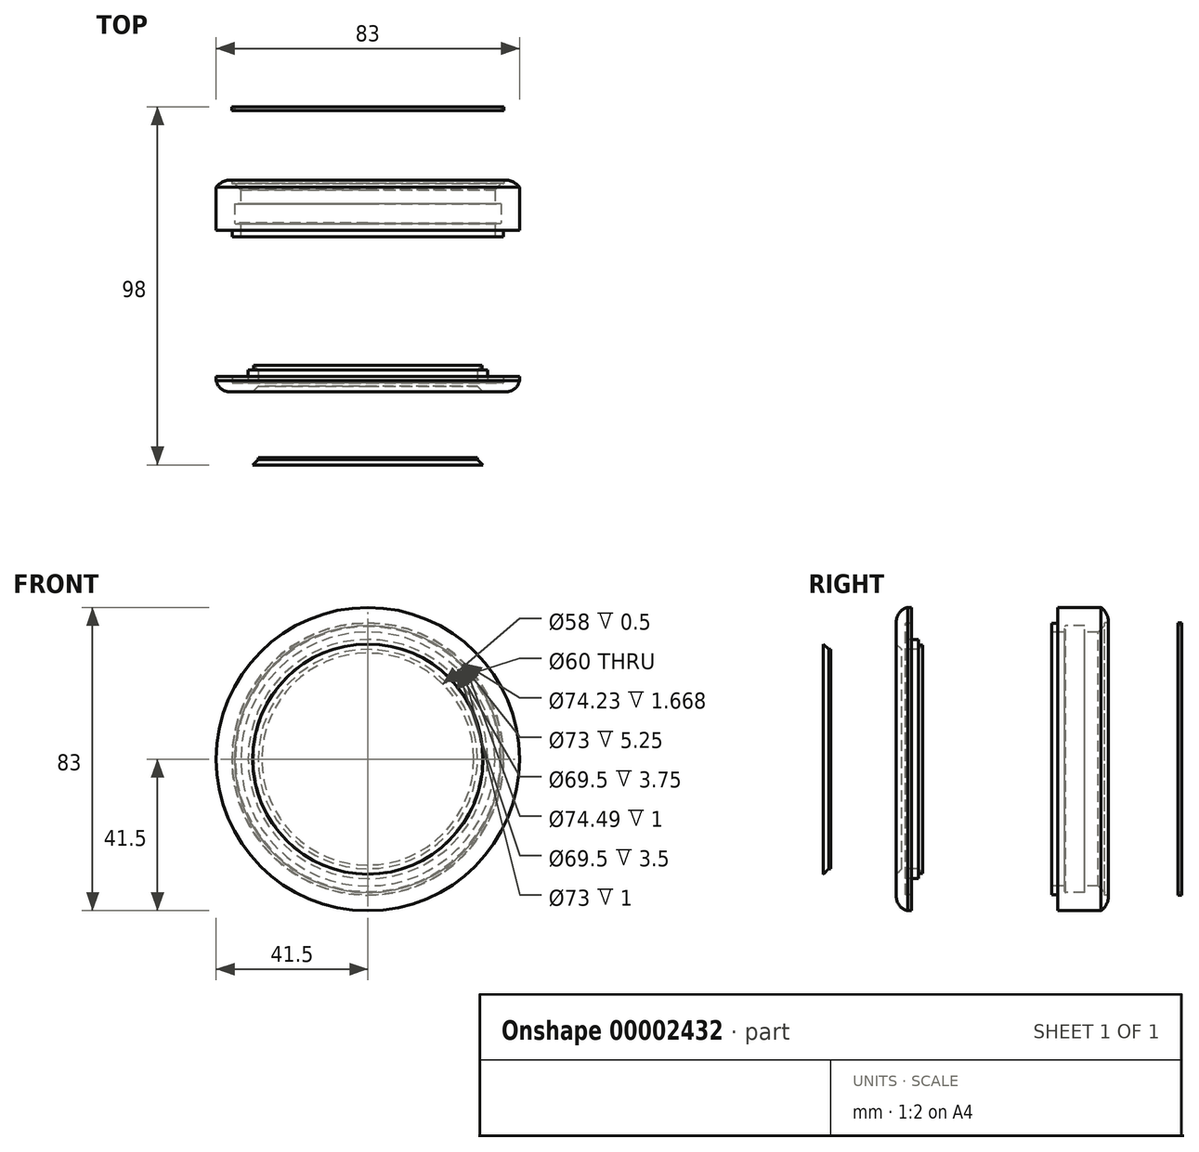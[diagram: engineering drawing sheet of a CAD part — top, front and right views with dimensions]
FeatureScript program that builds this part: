
annotation { "Feature Type Name" : "Feature", "Feature Type Description" : "" }
export const myFeature = defineFeature(function(context is Context, id is Id, definition is map)
    precondition{}
    {
        {
            var Q0;
            Q0=qCreatedBy(makeId("Top.planeOp"),FACE);
            var sketch = newSketch(context, id + "F0", { "sketchPlane" : qUnion([Q0])});
            skLineSegment(sketch, "E0", {"start": v(-33.25, 2.75) * mm, "end": v(-34.25, 2.75) * mm});
            skLineSegment(sketch, "E1.bottom", {"start": v(-34.25, 11.25) * mm, "end": v(-36, 11.25) * mm});
            skLineSegment(sketch, "E1.top", {"start": v(-34.25, 6.25) * mm, "end": v(-36, 6.25) * mm});
            skLineSegment(sketch, "E1.right", {"start": v(-36, 11.25) * mm, "end": v(-36, 6.25) * mm});
            skLineSegment(sketch, "E2.bottom", {"start": v(-33.25, 11.25) * mm, "end": v(-31.5, 11.25) * mm});
            skLineSegment(sketch, "E2.top", {"start": v(-33.25, 6.25) * mm, "end": v(-31.5, 6.25) * mm});
            skLineSegment(sketch, "E2.right", {"start": v(-31.5, 11.25) * mm, "end": v(-31.5, 6.25) * mm});
            skLineSegment(sketch, "E3", {"start": v(-41.5, 16) * mm, "end": v(-40, 16) * mm});
            skLineSegment(sketch, "E4", {"start": v(-40, 16) * mm, "end": v(-40, 9.75) * mm});
            skLineSegment(sketch, "E5", {"start": v(-40, 9.75) * mm, "end": v(-36.5, 6.25) * mm});
            skLineSegment(sketch, "E6", {"start": v(-36.5, 6.25) * mm, "end": v(-36.5, 9.75) * mm});
            skLineSegment(sketch, "E7", {"start": v(-36.5, 9.75) * mm, "end": v(-36.5, 11.5) * mm});
            skArc(sketch, "E8", {"start": v(-37.25, 18) * mm, "mid": v(-39.62, 17.53) * mm, "end": v(-41.5, 16) * mm});
            skLineSegment(sketch, "E9", {"start": v(-41.5, 16) * mm, "end": v(-41.5, 4.17) * mm});
            skLineSegment(sketch, "E10", {"start": v(-34.75, 2.5) * mm, "end": v(-34.75, 6) * mm});
            skLineSegment(sketch, "E11", {"start": v(-34.75, 6) * mm, "end": v(-36.25, 6) * mm});
            skLineSegment(sketch, "E12", {"start": v(-36.25, 6) * mm, "end": v(-40, 9.75) * mm});
            skLineSegment(sketch, "E13", {"start": v(-40, 9.75) * mm, "end": v(-40, 16) * mm});
            skLineSegment(sketch, "E14", {"start": v(-33.25, 14.75) * mm, "end": v(-33.25, 11.25) * mm});
            skLineSegment(sketch, "E15", {"start": v(-34.25, 14.75) * mm, "end": v(-34.25, 11.25) * mm});
            skLineSegment(sketch, "E16", {"start": v(-34.25, 6.25) * mm, "end": v(-34.25, 11.25) * mm});
            skLineSegment(sketch, "E17", {"start": v(-33.25, 2.75) * mm, "end": v(-33.25, 6.25) * mm});
            skLineSegment(sketch, "E18", {"start": v(-33.25, 11.25) * mm, "end": v(-33.25, 6.25) * mm});
            skLineSegment(sketch, "E19", {"start": v(-34.25, 6.25) * mm, "end": v(-34.25, 2.75) * mm});
            skLineSegment(sketch, "E20", {"start": v(-41.5, 0) * mm, "end": v(41.5, 0) * mm, "construction": true});
            skLineSegment(sketch, "E21", {"start": v(-41.5, 4.17) * mm, "end": v(-41.5, 3.08) * mm});
            skLineSegment(sketch, "E22", {"start": v(-37.68, 0) * mm, "end": v(0, 0) * mm});
            skLineSegment(sketch, "E23", {"start": v(-34.75, 2.5) * mm, "end": v(-32.75, 2.5) * mm});
            skLineSegment(sketch, "E24", {"start": v(-32.75, 2.5) * mm, "end": v(-32.75, 6) * mm});
            skLineSegment(sketch, "E25", {"start": v(-32.75, 6) * mm, "end": v(-31.23, 6) * mm});
            skLineSegment(sketch, "E26", {"start": v(-31.23, 6) * mm, "end": v(-31.23, 7.23) * mm});
            skLineSegment(sketch, "E27", {"start": v(-30, 6) * mm, "end": v(-30, 1.5) * mm});
            skLineSegment(sketch, "E28", {"start": v(0, 1.5) * mm, "end": v(0, 0) * mm});
            skLineSegment(sketch, "E29", {"start": v(-40, 9.75) * mm, "end": v(-36.5, 9.75) * mm, "construction": true});
            skLineSegment(sketch, "E30", {"start": v(-36.5, 6.25) * mm, "end": v(-36, 6.25) * mm, "construction": true});
            skLineSegment(sketch, "E31", {"start": v(-41.5, 0) * mm, "end": v(-41.5, 18) * mm, "construction": true});
            skLineSegment(sketch, "E32", {"start": v(-33.52, 15) * mm, "end": v(-33.52, 14.75) * mm, "construction": true});
            skLineSegment(sketch, "E33", {"start": v(-33.75, 2.75) * mm, "end": v(-33.75, 2.5) * mm, "construction": true});
            skLineSegment(sketch, "E34", {"start": v(-37.25, 17) * mm, "end": v(-36.5, 17) * mm});
            skLineSegment(sketch, "E35", {"start": v(-41.5, 4.17) * mm, "end": v(-40.2, 4.17) * mm});
            skLineSegment(sketch, "E36", {"start": v(-40.2, 4.17) * mm, "end": v(-37.12, 4.17) * mm});
            skLineSegment(sketch, "E37", {"start": v(-37.12, 2.5) * mm, "end": v(-37.12, 4.17) * mm});
            skLineSegment(sketch, "E38", {"start": v(-37.12, 2.5) * mm, "end": v(-34.75, 2.5) * mm});
            skLineSegment(sketch, "E39", {"start": v(-33.25, 2.5) * mm, "end": v(-33.25, 0) * mm, "construction": true});
            skLineSegment(sketch, "E40", {"start": v(-44.1, 18) * mm, "end": v(-44.1, 17) * mm, "construction": true});
            skLineSegment(sketch, "E41", {"start": v(-44.1, 17) * mm, "end": v(-44.1, 16) * mm, "construction": true});
            skLineSegment(sketch, "E42", {"start": v(-44.1, 2.5) * mm, "end": v(-44.1, 1.5) * mm, "construction": true});
            skLineSegment(sketch, "E43", {"start": v(-44.1, 16) * mm, "end": v(-44.1, 11.5) * mm, "construction": true});
            skLineSegment(sketch, "E44", {"start": v(-44.1, 4.17) * mm, "end": v(-44.1, 2.5) * mm, "construction": true});
            skLineSegment(sketch, "E45", {"start": v(-37.25, 18) * mm, "end": v(-37.25, 17) * mm});
            skLineSegment(sketch, "E46", {"start": v(-41.5, 21.17) * mm, "end": v(-37.25, 21.17) * mm, "construction": true});
            skLineSegment(sketch, "E47", {"start": v(-37.25, 21.17) * mm, "end": v(-34.75, 21.17) * mm, "construction": true});
            skLineSegment(sketch, "E48", {"start": v(-34.75, 21.17) * mm, "end": v(-32.75, 21.17) * mm, "construction": true});
            skLineSegment(sketch, "E49", {"start": v(-30, 21.17) * mm, "end": v(-23.5, 21.17) * mm, "construction": true});
            skLineSegment(sketch, "E50", {"start": v(-23.5, 21.17) * mm, "end": v(0, 21.17) * mm, "construction": true});
            skLineSegment(sketch, "E51", {"start": v(-30, 6) * mm, "end": v(-31.23, 7.23) * mm});
            skLineSegment(sketch, "E52", {"start": v(-33.25, 4.5) * mm, "end": v(-32.75, 4.5) * mm, "construction": true});
            skLineSegment(sketch, "E53", {"start": v(-34.25, 4.5) * mm, "end": v(-34.75, 4.5) * mm, "construction": true});
            skLineSegment(sketch, "E54", {"start": v(-30, 1.5) * mm, "end": v(-31.5, 0) * mm});
            skLineSegment(sketch, "E55", {"start": v(0, 0) * mm, "end": v(0, 18) * mm, "construction": true});
            skLineSegment(sketch, "E56", {"start": v(-34.75, 11.5) * mm, "end": v(-36.5, 11.5) * mm});
            skLineSegment(sketch, "E57", {"start": v(-34.75, 11.5) * mm, "end": v(-34.75, 15.25) * mm});
            skLineSegment(sketch, "E58", {"start": v(-34.75, 15.25) * mm, "end": v(-36.5, 17) * mm});
            skLineSegment(sketch, "E59", {"start": v(-33.25, 14.75) * mm, "end": v(-34.25, 14.75) * mm});
            skLineSegment(sketch, "E60", {"start": v(-44.1, 6) * mm, "end": v(-44.1, 4.17) * mm, "construction": true});
            skLineSegment(sketch, "E61", {"start": v(-44.1, 7.23) * mm, "end": v(-44.1, 6) * mm, "construction": true});
            skLineSegment(sketch, "E62", {"start": v(-44.1, 7.23) * mm, "end": v(-31.23, 7.23) * mm, "construction": true});
            skLineSegment(sketch, "E63", {"start": v(-44.1, 11.25) * mm, "end": v(-44.1, 7.23) * mm, "construction": true});
            skLineSegment(sketch, "E64", {"start": v(-44.1, 11.5) * mm, "end": v(-44.1, 11.25) * mm, "construction": true});
            skLineSegment(sketch, "E65", {"start": v(-47.67, 11.5) * mm, "end": v(-47.67, 6) * mm, "construction": true});
            skLineSegment(sketch, "E66", {"start": v(-30, 1.5) * mm, "end": v(-30, 2) * mm});
            skLineSegment(sketch, "E67", {"start": v(-30, 2) * mm, "end": v(-29, 2) * mm});
            skLineSegment(sketch, "E68", {"start": v(-29, 2) * mm, "end": v(-29, 1.5) * mm});
            skLineSegment(sketch, "E69", {"start": v(-29, 1.5) * mm, "end": v(0, 1.5) * mm});
            skLineSegment(sketch, "E70", {"start": v(-37.25, 18) * mm, "end": v(0, 18) * mm});
            skLineSegment(sketch, "E71", {"start": v(0, 18) * mm, "end": v(0, 15.25) * mm});
            skLineSegment(sketch, "E72", {"start": v(0, 15.25) * mm, "end": v(-34.75, 15.25) * mm});
            skLineSegment(sketch, "E73", {"start": v(-44.1, 1.5) * mm, "end": v(-44.1, 0) * mm, "construction": true});
            skLineSegment(sketch, "E74", {"start": v(-47.34, 0) * mm, "end": v(-47.34, 2.5) * mm, "construction": true});
            skArc(sketch, "E75", {"start": v(-41.5, 3.08) * mm, "mid": v(-40.13, 0.87) * mm, "end": v(-37.68, 0) * mm});
            skLineSegment(sketch, "E76", {"start": v(-32.75, 21.17) * mm, "end": v(-30, 21.17) * mm, "construction": true});
            skLineSegment(sketch, "E77", {"start": v(-36.5, 11.5) * mm, "end": v(-40, 11.5) * mm});
            skLineSegment(sketch, "E78", {"start": v(-36.5, 17) * mm, "end": v(-36.5, 18) * mm});
            skLineSegment(sketch, "E79", {"start": v(-36.5, 18) * mm, "end": v(-7.22, 18) * mm});
            skLineSegment(sketch, "E80", {"start": v(-7.22, 18) * mm, "end": v(-7.22, 19.47) * mm});
            skLineSegment(sketch, "E81", {"start": v(-7.22, 19.47) * mm, "end": v(-35.97, 19.47) * mm});
            skLineSegment(sketch, "E82", {"start": v(-35.97, 19.47) * mm, "end": v(-37.25, 18) * mm});
            skSolve(sketch);
        }
        {
            var Q0;
            Q0=makeQuery(id+"F0.imprint","IMPRINT",FACE,{"disambiguationData":[TD([[makeQuery(id+"F0.imprint","IMPRINT",EDGE,{"derivedFrom":sQuery(id+"F0.wireOp",EDGE,"E34")}),1.0]])]});
            var Q1;
            Q1=sQuery(id+"F0.wireOp",EDGE,"E55");
            revolve(context, id + "F1", {"entities" : qUnion([Q0]), "axis" : qUnion([Q1]), "revolveType" : RevolveType.FULL});
        }
        {
            var Q0;
            {var subQ2=sQuery(id+"F0.wireOp",EDGE,"E3");Q0=makeQuery(id+"F0.imprint","IMPRINT",FACE,{"disambiguationData":[TD([[makeQuery(id+"F0.imprint","IMPRINT",EDGE,{"derivedFrom":subQ2}),1.0]])]});}
            var Q1;
            {var subQ4=sQuery(id+"F0.wireOp",EDGE,"E6");Q1=makeQuery(id+"F0.imprint","IMPRINT",FACE,{"disambiguationData":[TD([[makeQuery(id+"F0.imprint","IMPRINT",EDGE,{"derivedFrom":subQ4}),1.0]])]});}
            var Q2;
            Q2=sQuery(id+"F0.wireOp",EDGE,"E55");
            revolve(context, id + "F2", {"entities" : qUnion([Q0, Q1]), "axis" : qUnion([Q2]), "revolveType" : RevolveType.FULL});
        }
        {
            var Q0;
            {var subQ2=sQuery(id+"F0.wireOp",EDGE,"E3");Q0=makeQuery(id+"F0.imprint","IMPRINT",FACE,{"disambiguationData":[TD([[makeQuery(id+"F0.imprint","IMPRINT",EDGE,{"derivedFrom":subQ2}),-1.0]])]});}
            var Q1;
            Q1=sQuery(id+"F0.wireOp",EDGE,"E9");
            var Q2;
            Q2=sQuery(id+"F0.wireOp",EDGE,"E3");
            var Q3;
            Q3=sQuery(id+"F0.wireOp",EDGE,"E4");
            var Q4;
            Q4=sQuery(id+"F0.wireOp",EDGE,"E5");
            var Q5;
            Q5=sQuery(id+"F0.wireOp",EDGE,"E11");
            var Q6;
            Q6=sQuery(id+"F0.wireOp",EDGE,"E10");
            var Q7;
            Q7=sQuery(id+"F0.wireOp",EDGE,"E38");
            var Q8;
            Q8=sQuery(id+"F0.wireOp",EDGE,"E37");
            var Q9;
            Q9=sQuery(id+"F0.wireOp",EDGE,"E36");
            var Q10;
            Q10=sQuery(id+"F0.wireOp",EDGE,"E35");
            var Q11;
            Q11=sQuery(id+"F0.wireOp",EDGE,"E55");
            revolve(context, id + "F3", {"operationType" : NewBodyOperationType.ADD, "entities" : qUnion([Q0]), "surfaceEntities" : qUnion([Q1, Q2, Q3, Q4, Q5, Q6, Q7, Q8, Q9, Q10]), "axis" : qUnion([Q11]), "revolveType" : RevolveType.FULL});
        }
        {
            var Q0;
            Q0=makeQuery(id+"F0.imprint","IMPRINT",FACE,{"disambiguationData":[TD([[makeQuery(id+"F0.imprint","IMPRINT",EDGE,{"derivedFrom":sQuery(id+"F0.wireOp",EDGE,"E21")}),1.0]])]});
            var Q1;
            Q1=sQuery(id+"F0.wireOp",EDGE,"E55");
            revolve(context, id + "F4", {"entities" : qUnion([Q0]), "axis" : qUnion([Q1]), "revolveType" : RevolveType.FULL});
        }
        {
            var Q0;
            {var subQ1=sQuery(id+"F0.wireOp",EDGE,"E28");Q0=makeQuery(id+"F0.imprint","IMPRINT",FACE,{"disambiguationData":[TD([[makeQuery(id+"F0.imprint","IMPRINT",EDGE,{"derivedFrom":subQ1}),-1.0]])]});}
            var Q1;
            Q1=sQuery(id+"F0.wireOp",EDGE,"E55");
            revolve(context, id + "F5", {"entities" : qUnion([Q0]), "axis" : qUnion([Q1]), "revolveType" : RevolveType.FULL});
        }
        {
            var Q0;
            Q0=makeQuery(id+"F4.opRevolve","SWEPT_BODY",BODY,{"disambiguationData":[OSD([sQuery(id+"F0.wireOp",EDGE,"E21"),sQuery(id+"F0.wireOp",EDGE,"E22"),sQuery(id+"F0.wireOp",EDGE,"E23"),sQuery(id+"F0.wireOp",EDGE,"E24"),sQuery(id+"F0.wireOp",EDGE,"E25"),sQuery(id+"F0.wireOp",EDGE,"E26"),sQuery(id+"F0.wireOp",EDGE,"E27"),sQuery(id+"F0.wireOp",EDGE,"E35"),sQuery(id+"F0.wireOp",EDGE,"E36"),sQuery(id+"F0.wireOp",EDGE,"E37"),sQuery(id+"F0.wireOp",EDGE,"E38"),sQuery(id+"F0.wireOp",EDGE,"E51"),sQuery(id+"F0.wireOp",EDGE,"E54"),sQuery(id+"F0.wireOp",EDGE,"E66"),sQuery(id+"F0.wireOp",EDGE,"E75")])]});
            var Q1;
            Q1=makeQuery(id+"F3.opRevolve","SWEPT_BODY",BODY,{"disambiguationData":[OSD([sQuery(id+"F0.wireOp",EDGE,"E3"),sQuery(id+"F0.wireOp",EDGE,"E9"),sQuery(id+"F0.wireOp",EDGE,"E10"),sQuery(id+"F0.wireOp",EDGE,"E11"),sQuery(id+"F0.wireOp",EDGE,"E12"),sQuery(id+"F0.wireOp",EDGE,"E13"),sQuery(id+"F0.wireOp",EDGE,"E35"),sQuery(id+"F0.wireOp",EDGE,"E36"),sQuery(id+"F0.wireOp",EDGE,"E37"),sQuery(id+"F0.wireOp",EDGE,"E38")])]});
            var Q2;
            Q2=makeQuery(id+"F2.opRevolve","SWEPT_BODY",BODY,{"disambiguationData":[OSD([sQuery(id+"F0.wireOp",EDGE,"E3"),sQuery(id+"F0.wireOp",EDGE,"E6"),sQuery(id+"F0.wireOp",EDGE,"E7"),sQuery(id+"F0.wireOp",EDGE,"E8"),sQuery(id+"F0.wireOp",EDGE,"E12"),sQuery(id+"F0.wireOp",EDGE,"E13"),sQuery(id+"F0.wireOp",EDGE,"E34"),sQuery(id+"F0.wireOp",EDGE,"E45"),sQuery(id+"F0.wireOp",EDGE,"E56"),sQuery(id+"F0.wireOp",EDGE,"E57"),sQuery(id+"F0.wireOp",EDGE,"E58")])]});
            var Q3;
            Q3=makeQuery(id+"F1.opRevolve","SWEPT_BODY",BODY,{"disambiguationData":[OSD([sQuery(id+"F0.wireOp",EDGE,"E34"),sQuery(id+"F0.wireOp",EDGE,"E45"),sQuery(id+"F0.wireOp",EDGE,"E70"),sQuery(id+"F0.wireOp",EDGE,"E78")])]});
            transform(context, id + "F6", {"entities" : qUnion([Q0, Q1, Q2, Q3]), "transformType" : TransformType.TRANSLATION_3D, "dx" : 0 * mm, "dy" : 20 * mm, "dz" : 0 * mm, "makeCopy" : false});
        }
        {
            var Q0;
            Q0=makeQuery(id+"F3.opRevolve","SWEPT_BODY",BODY,{"disambiguationData":[OSD([sQuery(id+"F0.wireOp",EDGE,"E3"),sQuery(id+"F0.wireOp",EDGE,"E9"),sQuery(id+"F0.wireOp",EDGE,"E10"),sQuery(id+"F0.wireOp",EDGE,"E11"),sQuery(id+"F0.wireOp",EDGE,"E12"),sQuery(id+"F0.wireOp",EDGE,"E13"),sQuery(id+"F0.wireOp",EDGE,"E35"),sQuery(id+"F0.wireOp",EDGE,"E36"),sQuery(id+"F0.wireOp",EDGE,"E37"),sQuery(id+"F0.wireOp",EDGE,"E38")])]});
            var Q1;
            Q1=makeQuery(id+"F1.opRevolve","SWEPT_BODY",BODY,{"disambiguationData":[OSD([sQuery(id+"F0.wireOp",EDGE,"E34"),sQuery(id+"F0.wireOp",EDGE,"E45"),sQuery(id+"F0.wireOp",EDGE,"E70"),sQuery(id+"F0.wireOp",EDGE,"E78")])]});
            var Q2;
            Q2=makeQuery(id+"F2.opRevolve","SWEPT_BODY",BODY,{"disambiguationData":[OSD([sQuery(id+"F0.wireOp",EDGE,"E3"),sQuery(id+"F0.wireOp",EDGE,"E6"),sQuery(id+"F0.wireOp",EDGE,"E7"),sQuery(id+"F0.wireOp",EDGE,"E8"),sQuery(id+"F0.wireOp",EDGE,"E12"),sQuery(id+"F0.wireOp",EDGE,"E13"),sQuery(id+"F0.wireOp",EDGE,"E34"),sQuery(id+"F0.wireOp",EDGE,"E45"),sQuery(id+"F0.wireOp",EDGE,"E56"),sQuery(id+"F0.wireOp",EDGE,"E57"),sQuery(id+"F0.wireOp",EDGE,"E58")])]});
            transform(context, id + "F7", {"entities" : qUnion([Q0, Q1, Q2]), "transformType" : TransformType.TRANSLATION_3D, "dx" : 0 * mm, "dy" : 20 * mm, "dz" : 0 * mm, "makeCopy" : false});
        }
        {
            var Q0;
            Q0=makeQuery(id+"F1.opRevolve","SWEPT_BODY",BODY,{"disambiguationData":[OSD([sQuery(id+"F0.wireOp",EDGE,"E34"),sQuery(id+"F0.wireOp",EDGE,"E45"),sQuery(id+"F0.wireOp",EDGE,"E70"),sQuery(id+"F0.wireOp",EDGE,"E78")])]});
            var Q1;
            Q1=makeQuery(id+"F2.opRevolve","SWEPT_BODY",BODY,{"disambiguationData":[OSD([sQuery(id+"F0.wireOp",EDGE,"E3"),sQuery(id+"F0.wireOp",EDGE,"E6"),sQuery(id+"F0.wireOp",EDGE,"E7"),sQuery(id+"F0.wireOp",EDGE,"E8"),sQuery(id+"F0.wireOp",EDGE,"E12"),sQuery(id+"F0.wireOp",EDGE,"E13"),sQuery(id+"F0.wireOp",EDGE,"E34"),sQuery(id+"F0.wireOp",EDGE,"E45"),sQuery(id+"F0.wireOp",EDGE,"E56"),sQuery(id+"F0.wireOp",EDGE,"E57"),sQuery(id+"F0.wireOp",EDGE,"E58")])]});
            transform(context, id + "F8", {"entities" : qUnion([Q0, Q1]), "transformType" : TransformType.TRANSLATION_3D, "dx" : 0 * mm, "dy" : 20 * mm, "dz" : 0 * mm, "makeCopy" : false});
        }
        {
            var Q0;
            Q0=makeQuery(id+"F1.opRevolve","SWEPT_BODY",BODY,{"disambiguationData":[OSD([sQuery(id+"F0.wireOp",EDGE,"E34"),sQuery(id+"F0.wireOp",EDGE,"E45"),sQuery(id+"F0.wireOp",EDGE,"E70"),sQuery(id+"F0.wireOp",EDGE,"E78")])]});
            transform(context, id + "F9", {"entities" : qUnion([Q0]), "transformType" : TransformType.TRANSLATION_3D, "dx" : 0 * mm, "dy" : 20 * mm, "dz" : 0 * mm, "makeCopy" : false});
        }
    });
